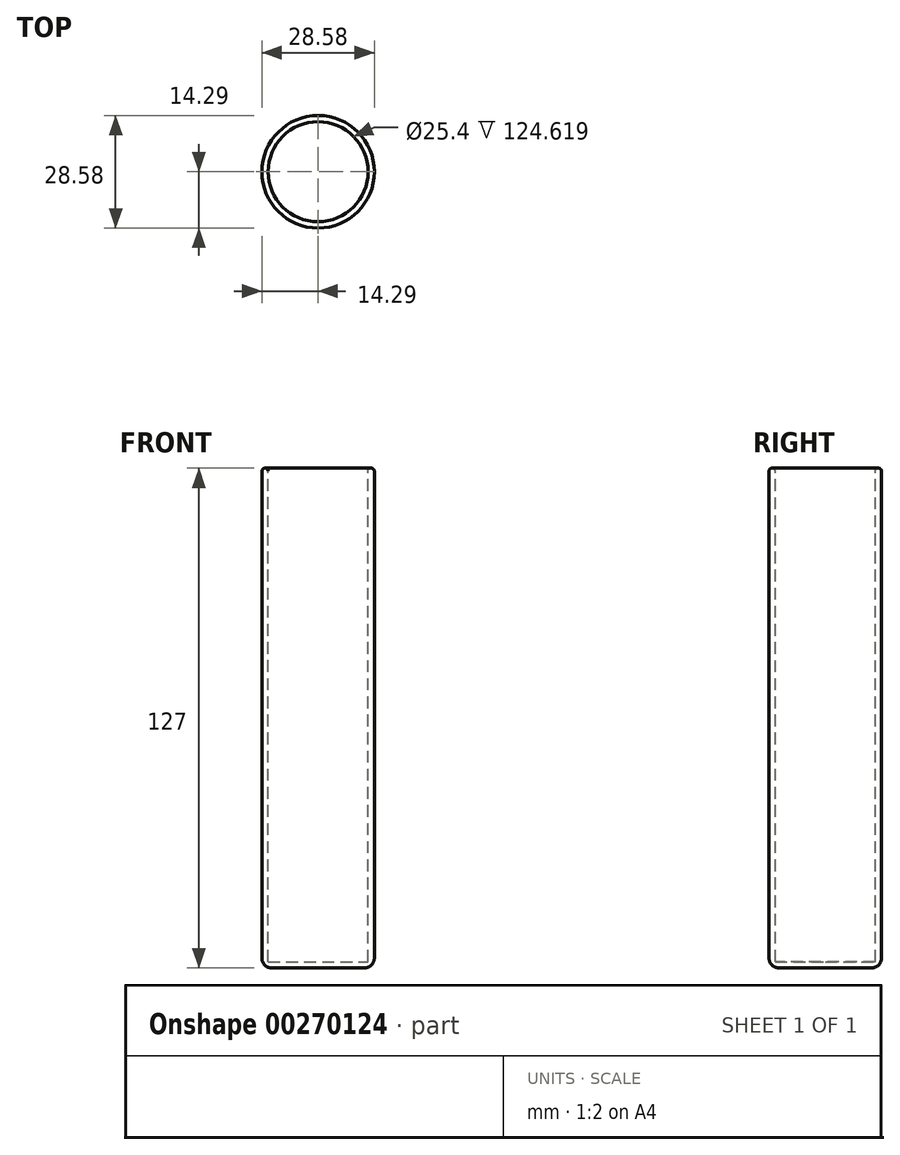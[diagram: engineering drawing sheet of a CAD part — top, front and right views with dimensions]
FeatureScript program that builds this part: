
annotation { "Feature Type Name" : "Feature", "Feature Type Description" : "" }
export const myFeature = defineFeature(function(context is Context, id is Id, definition is map)
    precondition{}
    {
        {
            var Q0;
            Q0=qCreatedBy(makeId("Front.planeOp"),FACE);
            var sketch = newSketch(context, id + "F0", { "sketchPlane" : qUnion([Q0])});
            skLineSegment(sketch, "E0.bottom", {"start": v(0, 6) * mm, "end": v(0, 6) * mm});
            skLineSegment(sketch, "E0.top", {"start": v(0, -6) * mm, "end": v(0, -6) * mm});
            skPoint(sketch, "E0.middle", {"position": v(0, 0) * mm});
            skLineSegment(sketch, "E1.right", {"start": v(14.29, 63.5) * mm, "end": v(14.29, -63.5) * mm});
            skLineSegment(sketch, "E2", {"start": v(0, 63.5) * mm, "end": v(0, -63.5) * mm});
            skLineSegment(sketch, "E3", {"start": v(14.29, 63.5) * mm, "end": v(0, 63.5) * mm});
            skLineSegment(sketch, "E4", {"start": v(14.29, -63.5) * mm, "end": v(0, -63.5) * mm});
            skSolve(sketch);
        }
        {
            var Q0;
            Q0=makeQuery(id+"F0.imprint","IMPRINT",FACE,{"disambiguationData":[TD([[makeQuery(id+"F0.imprint","IMPRINT",EDGE,{"derivedFrom":sQuery(id+"F0.wireOp",EDGE,"E1.right")}),-1.0]])]});
            var Q1;
            Q1=sQuery(id+"F0.wireOp",EDGE,"E2");
            revolve(context, id + "F1", {"entities" : qUnion([Q0]), "axis" : qUnion([Q1]), "revolveType" : RevolveType.FULL});
        }
        {
            var Q0;
            Q0=makeQuery(id+"F1.opRevolve","SWEPT_FACE",FACE,{"disambiguationData":[OSD([sQuery(id+"F0.wireOp",EDGE,"E3")])]});
            shell(context, id + "F2", {"entities" : qUnion([Q0]), "thickness" : 1.59 * mm});
        }
        {
            var Q0;
            Q0=makeQuery(id+"F1.opRevolve","SWEPT_EDGE",EDGE,{"disambiguationData":[OSD([sQuery(id+"F0.wireOp",EDGE,"E1.right"),sQuery(id+"F0.wireOp",EDGE,"E4")])]});
            fillet(context, id + "F3", {"entities" : qUnion([Q0]), "radius" : 2.54 * mm, "tangentPropagation" : true, "allowEdgeOverflow" : false});
        }
        {
            var Q0;
            Q0=makeQuery(id+"F1.opRevolve","SWEPT_EDGE",EDGE,{"disambiguationData":[OSD([sQuery(id+"F0.wireOp",EDGE,"E1.right"),sQuery(id+"F0.wireOp",EDGE,"E3")])]});
            var Q1;
            Q1=makeQuery(id+"F2.opShell","OFFSET_EDGE",EDGE,{"disambiguationData":[OSD([sQuery(id+"F0.wireOp",EDGE,"E1.right"),sQuery(id+"F0.wireOp",EDGE,"E3")])]});
            fillet(context, id + "F4", {"entities" : qUnion([Q0, Q1]), "radius" : 0.8 * mm, "tangentPropagation" : true, "allowEdgeOverflow" : false});
        }
    });
